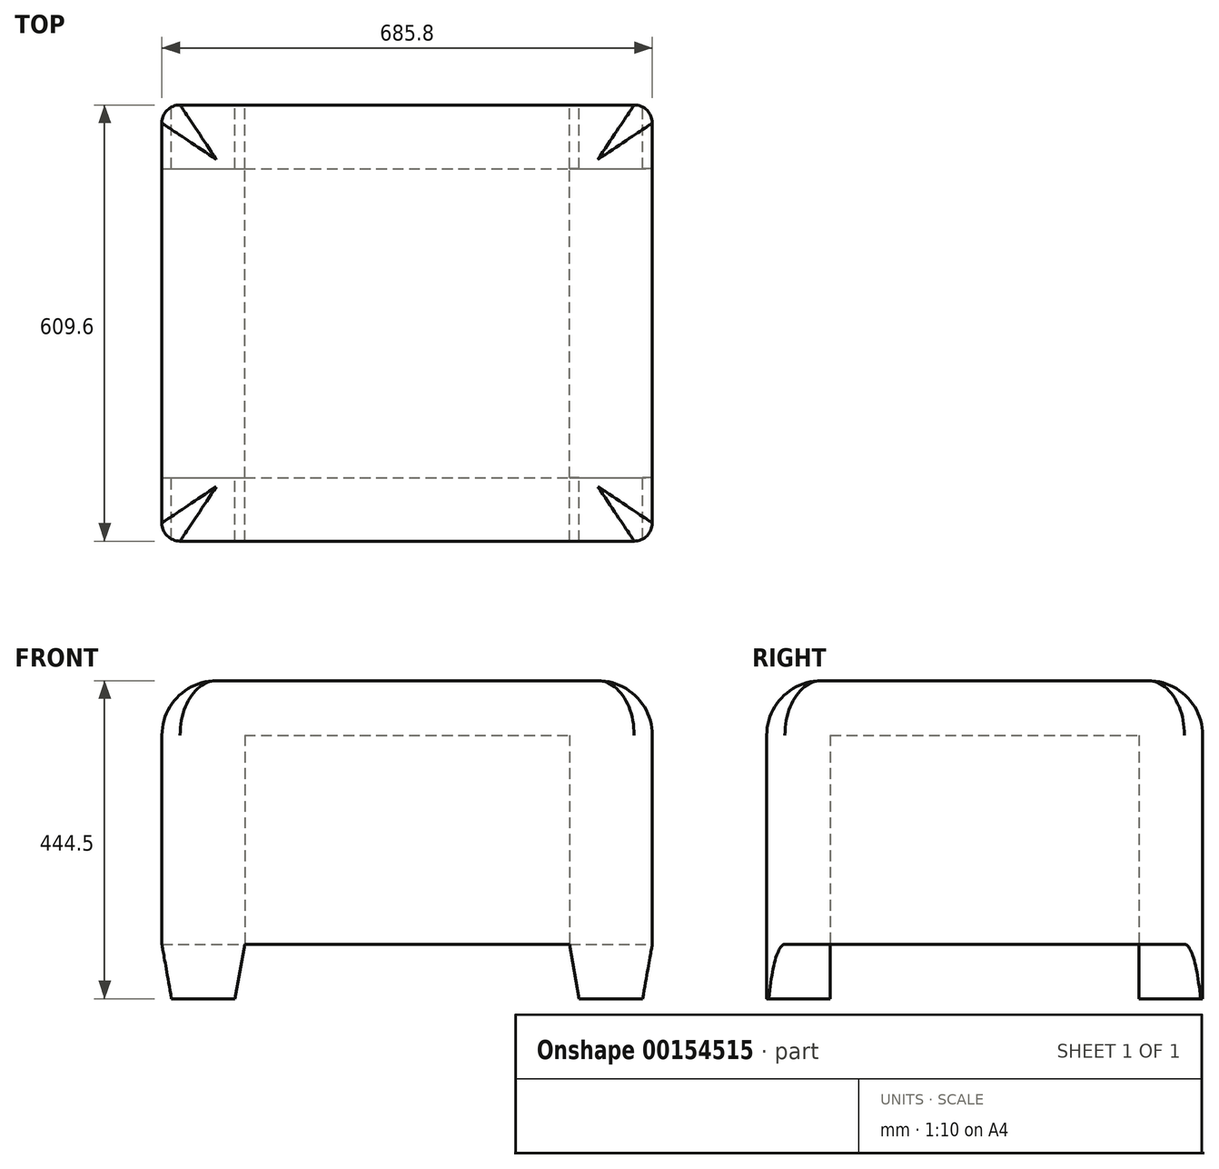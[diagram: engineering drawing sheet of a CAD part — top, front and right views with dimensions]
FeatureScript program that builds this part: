
annotation { "Feature Type Name" : "Feature", "Feature Type Description" : "" }
export const myFeature = defineFeature(function(context is Context, id is Id, definition is map)
    precondition{}
    {
        {
            var Q0;
            Q0=qCreatedBy(makeId("Front.planeOp"),FACE);
            var sketch = newSketch(context, id + "F0", { "sketchPlane" : qUnion([Q0])});
            skLineSegment(sketch, "E0", {"start": v(0, 0) * mm, "end": v(0, 368.3) * mm});
            skLineSegment(sketch, "E1", {"start": v(0, 368.3) * mm, "end": v(342.9, 368.3) * mm});
            skLineSegment(sketch, "E2", {"start": v(342.9, 368.3) * mm, "end": v(342.9, 0) * mm});
            skLineSegment(sketch, "E3", {"start": v(342.9, 0) * mm, "end": v(329.46, -76.2) * mm});
            skLineSegment(sketch, "E4", {"start": v(329.46, -76.2) * mm, "end": v(240.56, -76.2) * mm});
            skLineSegment(sketch, "E5", {"start": v(240.56, -76.2) * mm, "end": v(227.13, 0) * mm});
            skLineSegment(sketch, "E6", {"start": v(227.13, 0) * mm, "end": v(0, 0) * mm});
            skLineSegment(sketch, "E7.MirrorCS", {"start": v(0, 368.3) * mm, "end": v(-342.9, 368.3) * mm});
            skLineSegment(sketch, "E8.MirrorCS", {"start": v(-342.9, 368.3) * mm, "end": v(-342.9, 0) * mm});
            skLineSegment(sketch, "E9.MirrorCS", {"start": v(-342.9, 0) * mm, "end": v(-329.46, -76.2) * mm});
            skLineSegment(sketch, "E10.MirrorCS", {"start": v(-329.46, -76.2) * mm, "end": v(-240.56, -76.2) * mm});
            skLineSegment(sketch, "E11.MirrorCS", {"start": v(-240.56, -76.2) * mm, "end": v(-227.13, 0) * mm});
            skLineSegment(sketch, "E12.MirrorCS", {"start": v(-227.13, 0) * mm, "end": v(0, 0) * mm});
            skSolve(sketch);
        }
        {
            var Q0;
            Q0=makeQuery(id+"F0.imprint","IMPRINT",FACE,{"disambiguationData":[TD([[makeQuery(id+"F0.imprint","IMPRINT",EDGE,{"derivedFrom":sQuery(id+"F0.wireOp",EDGE,"E0")}),-1.0]])]});
            var Q1;
            Q1=makeQuery(id+"F0.imprint","IMPRINT",FACE,{"disambiguationData":[TD([[makeQuery(id+"F0.imprint","IMPRINT",EDGE,{"derivedFrom":sQuery(id+"F0.wireOp",EDGE,"E0")}),1.0]])]});
            extrude(context, id + "F1", {"entities" : qUnion([Q0, Q1]), "depth" : 609.6 * mm, "symmetric" : true});
        }
        {
            var Q0;
            Q0=qCreatedBy(makeId("Right.planeOp"),FACE);
            var sketch = newSketch(context, id + "F2", { "sketchPlane" : qUnion([Q0])});
            skLineSegment(sketch, "E13.bottom", {"start": v(-215.9, 0) * mm, "end": v(215.9, 0) * mm});
            skLineSegment(sketch, "E13.top", {"start": v(-215.9, -76.2) * mm, "end": v(215.9, -76.2) * mm});
            skLineSegment(sketch, "E13.left", {"start": v(-215.9, 0) * mm, "end": v(-215.9, -76.2) * mm});
            skLineSegment(sketch, "E13.right", {"start": v(215.9, 0) * mm, "end": v(215.9, -76.2) * mm});
            skSolve(sketch);
        }
        {
            var Q0;
            Q0 = qSketchRegion(id + "F2", true);
            extrude(context, id + "F3", {"entities" : qUnion([Q0]), "operationType" : NewBodyOperationType.REMOVE, "endBound" : BoundingType.THROUGH_ALL, "oppositeDirection" : true, "depth" : 30.48 * mm, "hasSecondDirection" : true, "secondDirectionBound" : BoundingType.THROUGH_ALL, "secondDirectionOppositeDirection" : false, "secondDirectionDepth" : 30.48 * mm});
        }
        {
            var Q0;
            Q0=makeQuery(id+"F1.opExtrude","SWEPT_FACE",FACE,{"disambiguationData":[OSD([sQuery(id+"F0.wireOp",EDGE,"E1"),sQuery(id+"F0.wireOp",EDGE,"E7.MirrorCS")])]});
            fillet(context, id + "F4", {"entities" : qUnion([Q0]), "radius" : 76.2 * mm, "tangentPropagation" : true, "allowEdgeOverflow" : false});
        }
        {
            var Q0;
            Q0=makeQuery(id+"F1.opExtrude","CAP_EDGE",EDGE,{"disambiguationData":[OSD([sQuery(id+"F0.wireOp",EDGE,"E2")])],"isStart":false});
            var Q1;
            {var subQ0=sQuery(id+"F0.wireOp",EDGE,"E1");Q1=makeQuery(id+"F4.opFillet","BLEND_EDGE",EDGE,{"blendedFrom":[makeQuery(id+"F1.opExtrude","SWEPT_EDGE",EDGE,{"disambiguationData":[OSD([subQ0,sQuery(id+"F0.wireOp",EDGE,"E2")])]}),makeQuery(id+"F1.opExtrude","CAP_EDGE",EDGE,{"disambiguationData":[OSD([subQ0,sQuery(id+"F0.wireOp",EDGE,"E7.MirrorCS")])],"isStart":false})],"blendedInto":[]});}
            var Q2;
            Q2=makeQuery(id+"F1.opExtrude","CAP_EDGE",EDGE,{"disambiguationData":[OSD([sQuery(id+"F0.wireOp",EDGE,"E2")])],"isStart":true});
            var Q3;
            {var subQ0=sQuery(id+"F0.wireOp",EDGE,"E1");Q3=makeQuery(id+"F4.opFillet","BLEND_EDGE",EDGE,{"blendedFrom":[makeQuery(id+"F1.opExtrude","SWEPT_EDGE",EDGE,{"disambiguationData":[OSD([subQ0,sQuery(id+"F0.wireOp",EDGE,"E2")])]}),makeQuery(id+"F1.opExtrude","CAP_EDGE",EDGE,{"disambiguationData":[OSD([subQ0,sQuery(id+"F0.wireOp",EDGE,"E7.MirrorCS")])],"isStart":true})],"blendedInto":[]});}
            var Q4;
            {var subQ0=sQuery(id+"F0.wireOp",EDGE,"E7.MirrorCS");Q4=makeQuery(id+"F4.opFillet","BLEND_EDGE",EDGE,{"blendedFrom":[makeQuery(id+"F1.opExtrude","SWEPT_EDGE",EDGE,{"disambiguationData":[OSD([subQ0,sQuery(id+"F0.wireOp",EDGE,"E8.MirrorCS")])]}),makeQuery(id+"F1.opExtrude","CAP_EDGE",EDGE,{"disambiguationData":[OSD([sQuery(id+"F0.wireOp",EDGE,"E1"),subQ0])],"isStart":true})],"blendedInto":[]});}
            var Q5;
            Q5=makeQuery(id+"F1.opExtrude","CAP_EDGE",EDGE,{"disambiguationData":[OSD([sQuery(id+"F0.wireOp",EDGE,"E8.MirrorCS")])],"isStart":true});
            var Q6;
            {var subQ0=sQuery(id+"F0.wireOp",EDGE,"E7.MirrorCS");Q6=makeQuery(id+"F4.opFillet","BLEND_EDGE",EDGE,{"blendedFrom":[makeQuery(id+"F1.opExtrude","SWEPT_EDGE",EDGE,{"disambiguationData":[OSD([subQ0,sQuery(id+"F0.wireOp",EDGE,"E8.MirrorCS")])]}),makeQuery(id+"F1.opExtrude","CAP_EDGE",EDGE,{"disambiguationData":[OSD([sQuery(id+"F0.wireOp",EDGE,"E1"),subQ0])],"isStart":false})],"blendedInto":[]});}
            var Q7;
            Q7=makeQuery(id+"F1.opExtrude","CAP_EDGE",EDGE,{"disambiguationData":[OSD([sQuery(id+"F0.wireOp",EDGE,"E8.MirrorCS")])],"isStart":false});
            fillet(context, id + "F5", {"entities" : qUnion([Q0, Q1, Q2, Q3, Q4, Q5, Q6, Q7]), "radius" : 25.4 * mm, "allowEdgeOverflow" : false});
        }
        {
            var Q0;
            Q0=makeQuery(id+"F3.boolean.opBoolean","MERGE",FACE,{"derivedFrom":[makeQuery(id+"F1.opExtrude","SWEPT_FACE",FACE,{"disambiguationData":[OSD([sQuery(id+"F0.wireOp",EDGE,"E6"),sQuery(id+"F0.wireOp",EDGE,"E12.MirrorCS")])]}),makeQuery(id+"F3.opExtrude","SWEPT_FACE",FACE,{"disambiguationData":[OSD([sQuery(id+"F2.wireOp",EDGE,"E13.bottom")])]})]});
            var sketch = newSketch(context, id + "F6", { "sketchPlane" : qUnion([Q0])});
            skLineSegment(sketch, "E14.bottom", {"start": v(-227.13, 215.9) * mm, "end": v(227.13, 215.9) * mm});
            skLineSegment(sketch, "E14.top", {"start": v(-227.13, -215.9) * mm, "end": v(227.13, -215.9) * mm});
            skLineSegment(sketch, "E14.left", {"start": v(-227.13, 215.9) * mm, "end": v(-227.13, -215.9) * mm});
            skLineSegment(sketch, "E14.right", {"start": v(227.13, 215.9) * mm, "end": v(227.13, -215.9) * mm});
            skSolve(sketch);
        }
        {
            var Q0;
            Q0=makeQuery(id+"F6.imprint","IMPRINT",FACE,{"disambiguationData":[TD([[makeQuery(id+"F6.imprint","IMPRINT",EDGE,{"derivedFrom":sQuery(id+"F6.wireOp",EDGE,"E14.bottom")}),-1.0]])]});
            extrude(context, id + "F7", {"entities" : qUnion([Q0]), "operationType" : NewBodyOperationType.REMOVE, "oppositeDirection" : true, "depth" : 292 * mm});
        }
    });
